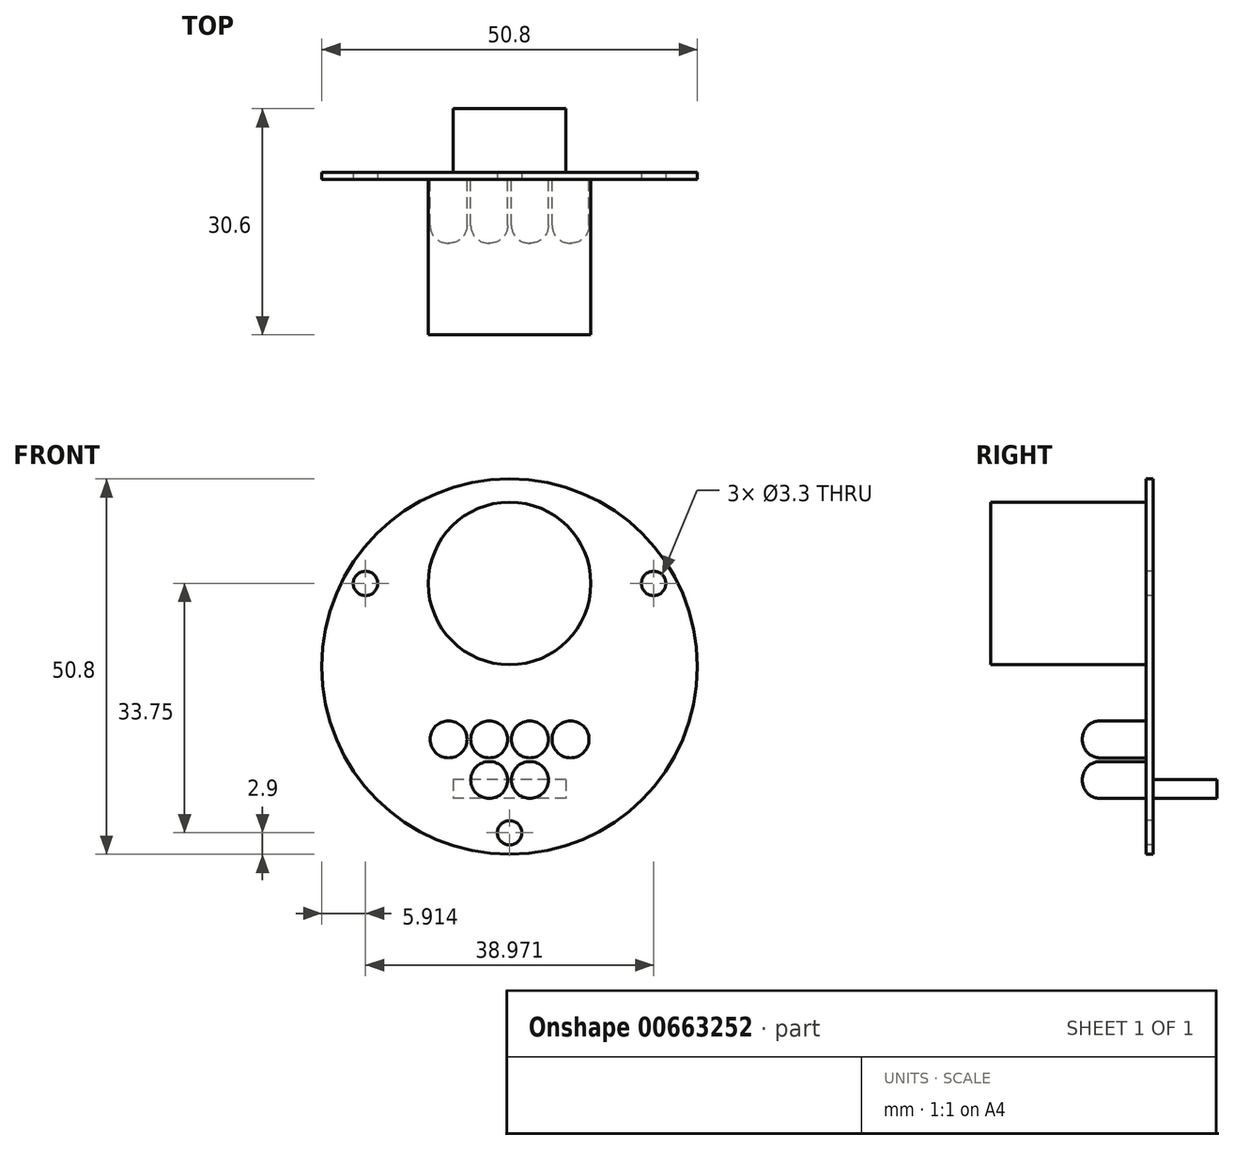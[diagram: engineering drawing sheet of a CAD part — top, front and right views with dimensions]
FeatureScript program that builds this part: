
annotation { "Feature Type Name" : "Feature", "Feature Type Description" : "" }
export const myFeature = defineFeature(function(context is Context, id is Id, definition is map)
    precondition{}
    {
        {
            var Q0;
            Q0=qCreatedBy(makeId("Front.planeOp"),FACE);
            var sketch = newSketch(context, id + "F0", { "sketchPlane" : qUnion([Q0])});
            skCircle(sketch, "E0", {"center": v(0, 0) * mm, "radius": 25.4 * mm});
            skSolve(sketch);
        }
        {
            var Q0;
            Q0 = qSketchRegion(id + "F0", true);
            extrude(context, id + "F1", {"entities" : qUnion([Q0]), "depth" : 1 * mm, "offsetDistance" : 25 * mm});
        }
        {
            var Q0;
            Q0=makeQuery(id+"F1.opExtrude","CAP_FACE",FACE,{"disambiguationData":[OSD([sQuery(id+"F0.wireOp",EDGE,"E0")])],"isStart":false});
            var sketch = newSketch(context, id + "F2", { "sketchPlane" : qUnion([Q0])});
            skLineSegment(sketch, "E1", {"start": v(0, 35.07) * mm, "end": v(0, -33.77) * mm, "construction": true});
            skCircle(sketch, "E2", {"center": v(-19.49, 11.25) * mm, "radius": 1.65 * mm});
            skCircle(sketch, "E3", {"center": v(0, 0) * mm, "radius": 22.5 * mm, "construction": true});
            skCircle(sketch, "E4", {"center": v(0, -22.5) * mm, "radius": 1.65 * mm});
            skCircle(sketch, "E5.MirrorC", {"center": v(19.49, 11.25) * mm, "radius": 1.65 * mm});
            skSolve(sketch);
        }
        {
            var Q0;
            Q0 = qSketchRegion(id + "F2", true);
            extrude(context, id + "F3", {"entities" : qUnion([Q0]), "operationType" : NewBodyOperationType.REMOVE, "endBound" : BoundingType.THROUGH_ALL, "oppositeDirection" : true, "depth" : 25 * mm, "offsetDistance" : 25 * mm});
        }
        {
            var Q0;
            Q0=makeQuery(id+"F1.opExtrude","CAP_FACE",FACE,{"disambiguationData":[OSD([sQuery(id+"F0.wireOp",EDGE,"E0")])],"isStart":false});
            var sketch = newSketch(context, id + "F4", { "sketchPlane" : qUnion([Q0])});
            skCircle(sketch, "E6", {"center": v(0, 11.25) * mm, "radius": 11 * mm});
            skCircle(sketch, "E7.0", {"center": v(0, -22.5) * mm, "radius": 1.65 * mm, "construction": true});
            skSolve(sketch);
        }
        {
            var Q0;
            Q0 = qSketchRegion(id + "F4", true);
            extrude(context, id + "F5", {"entities" : qUnion([Q0]), "operationType" : NewBodyOperationType.ADD, "depth" : 21 * mm, "offsetDistance" : 25 * mm});
        }
        {
            var Q0;
            Q0=makeQuery(id+"F1.opExtrude","CAP_FACE",FACE,{"disambiguationData":[OSD([sQuery(id+"F0.wireOp",EDGE,"E0")])],"isStart":false});
            var sketch = newSketch(context, id + "F6", { "sketchPlane" : qUnion([Q0])});
            skLineSegment(sketch, "E8", {"start": v(0, 23.74) * mm, "end": v(0, -28.68) * mm, "construction": true});
            skCircle(sketch, "E9", {"center": v(-8.25, -9.85) * mm, "radius": 2.5 * mm});
            skCircle(sketch, "E10", {"center": v(-2.75, -15.35) * mm, "radius": 2.5 * mm});
            skCircle(sketch, "E11", {"center": v(-2.75, -9.85) * mm, "radius": 2.5 * mm});
            skLineSegment(sketch, "E12", {"start": v(-14.85, -9.85) * mm, "end": v(24.8, -9.85) * mm, "construction": true});
            skLineSegment(sketch, "E13", {"start": v(-2.75, -16.1) * mm, "end": v(-2.75, -4.9) * mm, "construction": true});
            skCircle(sketch, "E14.MirrorC", {"center": v(2.75, -15.35) * mm, "radius": 2.5 * mm});
            skCircle(sketch, "E15.MirrorC", {"center": v(8.25, -9.85) * mm, "radius": 2.5 * mm});
            skCircle(sketch, "E16.MirrorC", {"center": v(2.75, -9.85) * mm, "radius": 2.5 * mm});
            skSolve(sketch);
        }
        {
            var Q0;
            Q0 = qSketchRegion(id + "F6", true);
            extrude(context, id + "F7", {"entities" : qUnion([Q0]), "operationType" : NewBodyOperationType.ADD, "depth" : 8.6 * mm, "offsetDistance" : 25 * mm});
        }
        {
            var Q0;
            Q0=makeQuery(id+"F7.opExtrude","CAP_FACE",FACE,{"disambiguationData":[OSD([sQuery(id+"F6.wireOp",EDGE,"E9")])],"isStart":false});
            var Q1;
            Q1=makeQuery(id+"F7.opExtrude","CAP_FACE",FACE,{"disambiguationData":[OSD([sQuery(id+"F6.wireOp",EDGE,"E11")])],"isStart":false});
            var Q2;
            Q2=makeQuery(id+"F7.opExtrude","CAP_FACE",FACE,{"disambiguationData":[OSD([sQuery(id+"F6.wireOp",EDGE,"E16.MirrorC")])],"isStart":false});
            var Q3;
            Q3=makeQuery(id+"F7.opExtrude","CAP_FACE",FACE,{"disambiguationData":[OSD([sQuery(id+"F6.wireOp",EDGE,"E15.MirrorC")])],"isStart":false});
            var Q4;
            Q4=makeQuery(id+"F7.opExtrude","CAP_FACE",FACE,{"disambiguationData":[OSD([sQuery(id+"F6.wireOp",EDGE,"E14.MirrorC")])],"isStart":false});
            var Q5;
            Q5=makeQuery(id+"F7.opExtrude","CAP_FACE",FACE,{"disambiguationData":[OSD([sQuery(id+"F6.wireOp",EDGE,"E10")])],"isStart":false});
            fillet(context, id + "F8", {"entities" : qUnion([Q0, Q1, Q2, Q3, Q4, Q5]), "radius" : 2.4 * mm, "tangentPropagation" : true, "allowEdgeOverflow" : false});
        }
        {
            var Q0;
            Q0=makeQuery(id+"F1.opExtrude","CAP_FACE",FACE,{"disambiguationData":[OSD([sQuery(id+"F0.wireOp",EDGE,"E0")])],"isStart":true});
            var sketch = newSketch(context, id + "F9", { "sketchPlane" : qUnion([Q0])});
            skLineSegment(sketch, "E17.bottom", {"start": v(-7.62, -15.3) * mm, "end": v(7.62, -15.3) * mm});
            skLineSegment(sketch, "E17.top", {"start": v(-7.62, -17.85) * mm, "end": v(7.62, -17.85) * mm});
            skLineSegment(sketch, "E17.left", {"start": v(-7.62, -15.3) * mm, "end": v(-7.62, -17.85) * mm});
            skLineSegment(sketch, "E17.right", {"start": v(7.62, -15.3) * mm, "end": v(7.62, -17.85) * mm});
            skSolve(sketch);
        }
        {
            var Q0;
            Q0 = qSketchRegion(id + "F9", true);
            extrude(context, id + "F10", {"entities" : qUnion([Q0]), "operationType" : NewBodyOperationType.ADD, "depth" : (30.6 - 21 - 1) * mm, "offsetDistance" : 25 * mm});
        }
    });
